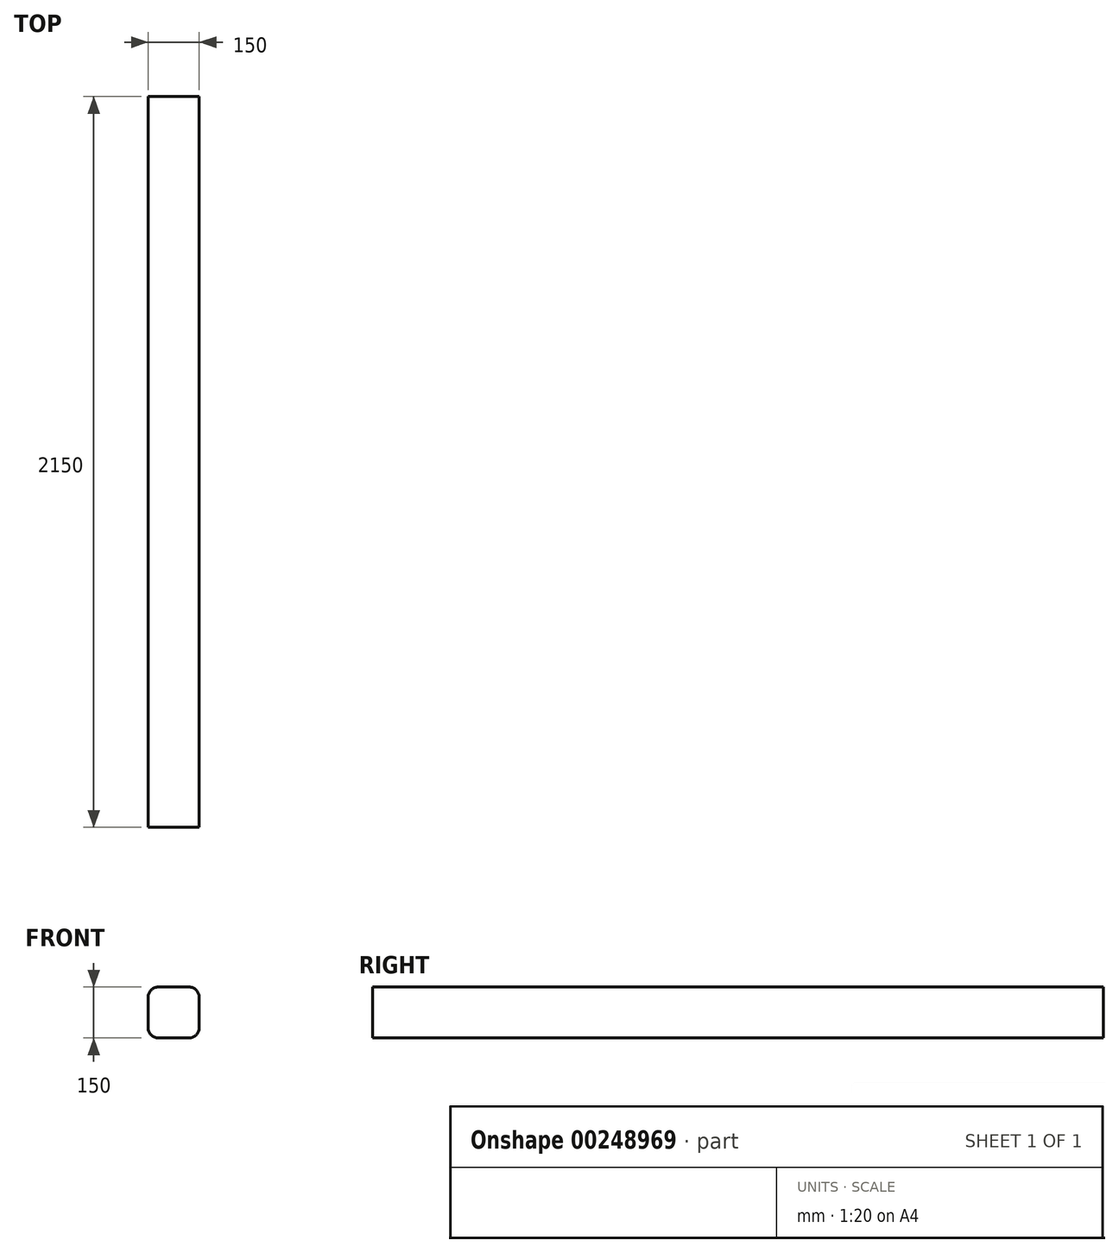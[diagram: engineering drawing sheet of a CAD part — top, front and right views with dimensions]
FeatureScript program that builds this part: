
annotation { "Feature Type Name" : "Feature", "Feature Type Description" : "" }
export const myFeature = defineFeature(function(context is Context, id is Id, definition is map)
    precondition{}
    {
        {
            var Q0;
            Q0=qCreatedBy(makeId("Front.planeOp"),FACE);
            var sketch = newSketch(context, id + "F0", { "sketchPlane" : qUnion([Q0])});
            skLineSegment(sketch, "E0.bottom", {"start": v(45, 75) * mm, "end": v(-45, 75) * mm});
            skLineSegment(sketch, "E0.top", {"start": v(45, -75) * mm, "end": v(-45, -75) * mm});
            skLineSegment(sketch, "E0.left", {"start": v(75, 45) * mm, "end": v(75, -45) * mm});
            skLineSegment(sketch, "E0.right", {"start": v(-75, 45) * mm, "end": v(-75, -45) * mm});
            skPoint(sketch, "E0.middle", {"position": v(0, 0) * mm});
            skPoint(sketch, "E1.visualSharp", {"position": v(75, 75) * mm});
            skArc(sketch, "E1.filletArc", {"start": v(75, 45) * mm, "mid": v(66.21, 66.21) * mm, "end": v(45, 75) * mm});
            skPoint(sketch, "E2.visualSharp", {"position": v(75, -75) * mm});
            skArc(sketch, "E2.filletArc", {"start": v(45, -75) * mm, "mid": v(66.21, -66.21) * mm, "end": v(75, -45) * mm});
            skPoint(sketch, "E3.visualSharp", {"position": v(-75, -75) * mm});
            skArc(sketch, "E3.filletArc", {"start": v(-75, -45) * mm, "mid": v(-66.21, -66.21) * mm, "end": v(-45, -75) * mm});
            skPoint(sketch, "E4.visualSharp", {"position": v(-75, 75) * mm});
            skArc(sketch, "E4.filletArc", {"start": v(-45, 75) * mm, "mid": v(-66.21, 66.21) * mm, "end": v(-75, 45) * mm});
            skSolve(sketch);
        }
        {
            var Q0;
            Q0 = qSketchRegion(id + "F0", true);
            extrude(context, id + "F1", {"entities" : qUnion([Q0]), "depth" : 2150 * mm});
        }
    });
